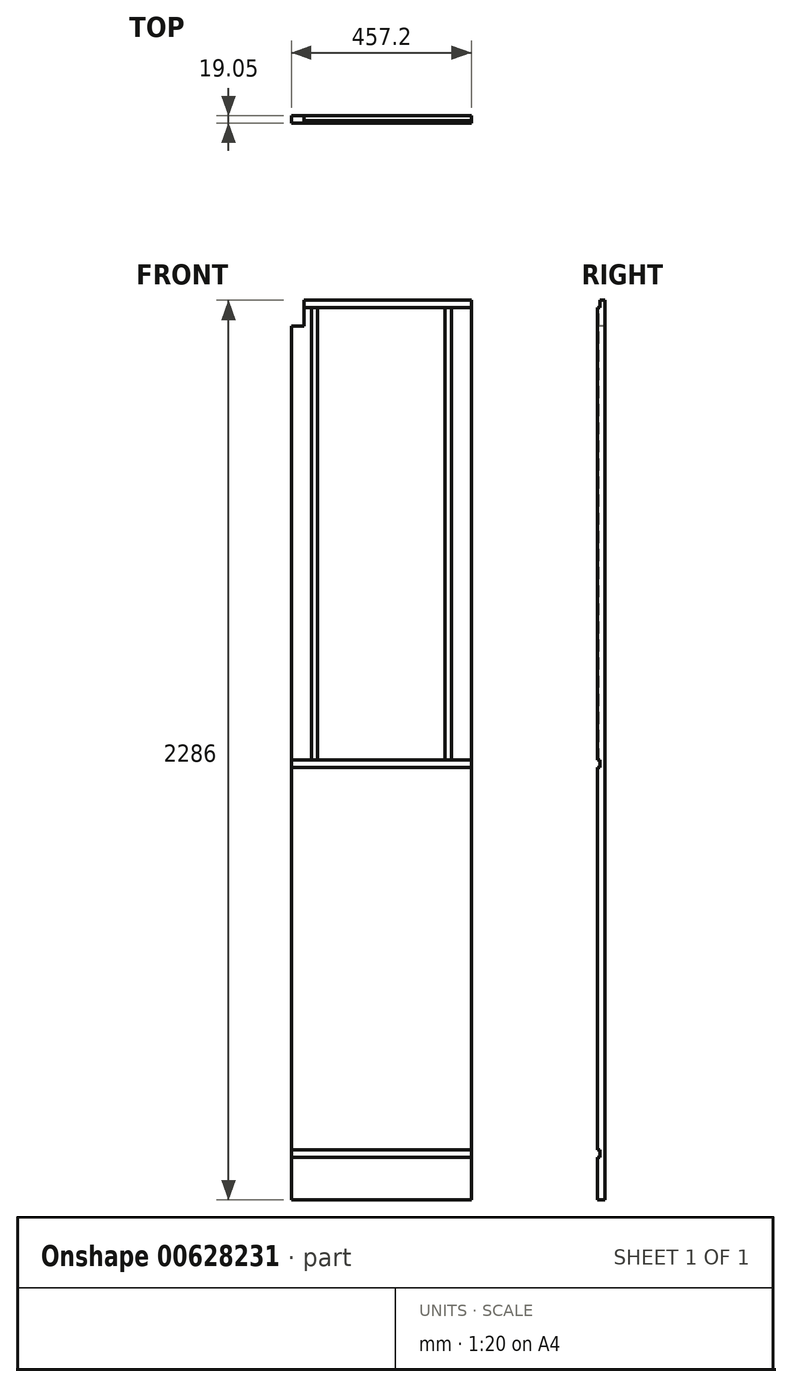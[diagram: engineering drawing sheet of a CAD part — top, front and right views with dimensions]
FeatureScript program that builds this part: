
annotation { "Feature Type Name" : "Feature", "Feature Type Description" : "" }
export const myFeature = defineFeature(function(context is Context, id is Id, definition is map)
    precondition{}
    {
        {
            var Q0;
            Q0=qCreatedBy(makeId("Front.planeOp"),FACE);
            var sketch = newSketch(context, id + "F0", { "sketchPlane" : qUnion([Q0])});
            skLineSegment(sketch, "E0.bottom", {"start": v(0, 0) * mm, "end": v(457.2, 0) * mm});
            skLineSegment(sketch, "E0.top", {"start": v(0, 2286) * mm, "end": v(457.2, 2286) * mm});
            skLineSegment(sketch, "E0.left", {"start": v(0, 0) * mm, "end": v(0, 2286) * mm});
            skLineSegment(sketch, "E0.right", {"start": v(457.2, 0) * mm, "end": v(457.2, 2286) * mm});
            skSolve(sketch);
        }
        {
            var Q0;
            Q0 = qSketchRegion(id + "F0", true);
            extrude(context, id + "F1", {"entities" : qUnion([Q0]), "depth" : 19.05 * mm, "offsetDistance" : 25.4 * mm});
        }
        {
            var Q0;
            Q0=makeQuery(id+"F1.opExtrude","CAP_FACE",FACE,{"disambiguationData":[OSD([sQuery(id+"F0.wireOp",EDGE,"E0.bottom"),sQuery(id+"F0.wireOp",EDGE,"E0.top"),sQuery(id+"F0.wireOp",EDGE,"E0.left"),sQuery(id+"F0.wireOp",EDGE,"E0.right")])],"isStart":false});
            var sketch = newSketch(context, id + "F2", { "sketchPlane" : qUnion([Q0])});
            skLineSegment(sketch, "E1.bottom", {"start": v(32, 2219.96) * mm, "end": v(0, 2219.96) * mm});
            skLineSegment(sketch, "E1.top", {"start": v(32, 2286) * mm, "end": v(0, 2286) * mm});
            skLineSegment(sketch, "E1.left", {"start": v(32, 2219.96) * mm, "end": v(32, 2286) * mm});
            skLineSegment(sketch, "E1.right", {"start": v(0, 2219.96) * mm, "end": v(0, 2286) * mm});
            skSolve(sketch);
        }
        {
            var Q0;
            Q0 = qSketchRegion(id + "F2", true);
            extrude(context, id + "F3", {"entities" : qUnion([Q0]), "operationType" : NewBodyOperationType.REMOVE, "endBound" : BoundingType.THROUGH_ALL, "oppositeDirection" : true, "depth" : 25.4 * mm, "offsetDistance" : 25.4 * mm});
        }
        {
            var Q0;
            Q0=makeQuery(id+"F1.opExtrude","CAP_FACE",FACE,{"disambiguationData":[OSD([sQuery(id+"F0.wireOp",EDGE,"E0.bottom"),sQuery(id+"F0.wireOp",EDGE,"E0.top"),sQuery(id+"F0.wireOp",EDGE,"E0.left"),sQuery(id+"F0.wireOp",EDGE,"E0.right")])],"isStart":false});
            var sketch = newSketch(context, id + "F4", { "sketchPlane" : qUnion([Q0])});
            skLineSegment(sketch, "E2.bottom", {"start": v(-11.67, 127) * mm, "end": v(519.07, 127) * mm});
            skLineSegment(sketch, "E2.top", {"start": v(-11.67, 107.7) * mm, "end": v(519.07, 107.7) * mm});
            skLineSegment(sketch, "E2.left", {"start": v(-11.67, 127) * mm, "end": v(-11.67, 107.7) * mm});
            skLineSegment(sketch, "E2.right", {"start": v(519.07, 127) * mm, "end": v(519.07, 107.7) * mm});
            skLineSegment(sketch, "E3.bottom", {"start": v(-24.94, 1117.6) * mm, "end": v(528.35, 1117.6) * mm});
            skLineSegment(sketch, "E3.top", {"start": v(-24.94, 1098.3) * mm, "end": v(528.35, 1098.3) * mm});
            skLineSegment(sketch, "E3.left", {"start": v(-24.94, 1117.6) * mm, "end": v(-24.94, 1098.3) * mm});
            skLineSegment(sketch, "E3.right", {"start": v(528.35, 1117.6) * mm, "end": v(528.35, 1098.3) * mm});
            skLineSegment(sketch, "E4.bottom", {"start": v(-16.64, 2295.24) * mm, "end": v(531.9, 2295.24) * mm});
            skLineSegment(sketch, "E4.top", {"start": v(-16.64, 2266.7) * mm, "end": v(531.9, 2266.7) * mm});
            skLineSegment(sketch, "E4.left", {"start": v(-16.64, 2295.24) * mm, "end": v(-16.64, 2266.7) * mm});
            skLineSegment(sketch, "E4.right", {"start": v(531.9, 2295.24) * mm, "end": v(531.9, 2266.7) * mm});
            skSolve(sketch);
        }
        {
            var Q0;
            Q0 = qSketchRegion(id + "F4", true);
            extrude(context, id + "F5", {"entities" : qUnion([Q0]), "operationType" : NewBodyOperationType.REMOVE, "oppositeDirection" : true, "depth" : 6.35 * mm, "offsetDistance" : 25.4 * mm});
        }
        {
            var Q0;
            {var subQ0=sQuery(id+"F0.wireOp",EDGE,"E0.left");var subQ1=sQuery(id+"F0.wireOp",EDGE,"E0.right");Q0=makeQuery(id+"F5.boolean.opBoolean","SPLIT",FACE,{"disambiguationData":[TD([makeQuery(id+"F5.opExtrude","SWEPT_FACE",FACE,{"disambiguationData":[OSD([sQuery(id+"F4.wireOp",EDGE,"E3.bottom")])]})])],"derivedFrom":makeQuery(id+"F1.opExtrude","CAP_FACE",FACE,{"disambiguationData":[OSD([sQuery(id+"F0.wireOp",EDGE,"E0.bottom"),sQuery(id+"F0.wireOp",EDGE,"E0.top"),subQ0,subQ1])],"isStart":false})});}
            var sketch = newSketch(context, id + "F6", { "sketchPlane" : qUnion([Q0])});
            skLineSegment(sketch, "E5.bottom", {"start": v(50.8, 1107.77) * mm, "end": v(66.68, 1107.77) * mm});
            skLineSegment(sketch, "E5.top", {"start": v(50.8, 2276.84) * mm, "end": v(66.68, 2276.84) * mm});
            skLineSegment(sketch, "E5.left", {"start": v(50.8, 1107.77) * mm, "end": v(50.8, 2276.84) * mm});
            skLineSegment(sketch, "E5.right", {"start": v(66.68, 1107.77) * mm, "end": v(66.68, 2276.84) * mm});
            skLineSegment(sketch, "E6.bottom", {"start": v(390.52, 1107.5) * mm, "end": v(406.4, 1107.5) * mm});
            skLineSegment(sketch, "E6.top", {"start": v(390.52, 2282.01) * mm, "end": v(406.4, 2282.01) * mm});
            skLineSegment(sketch, "E6.left", {"start": v(390.52, 1107.5) * mm, "end": v(390.52, 2282.01) * mm});
            skLineSegment(sketch, "E6.right", {"start": v(406.4, 1107.5) * mm, "end": v(406.4, 2282.01) * mm});
            skSolve(sketch);
        }
        {
            var Q0;
            Q0 = qSketchRegion(id + "F6", true);
            extrude(context, id + "F7", {"entities" : qUnion([Q0]), "operationType" : NewBodyOperationType.REMOVE, "oppositeDirection" : true, "depth" : 4.76 * mm, "offsetDistance" : 25.4 * mm});
        }
    });
